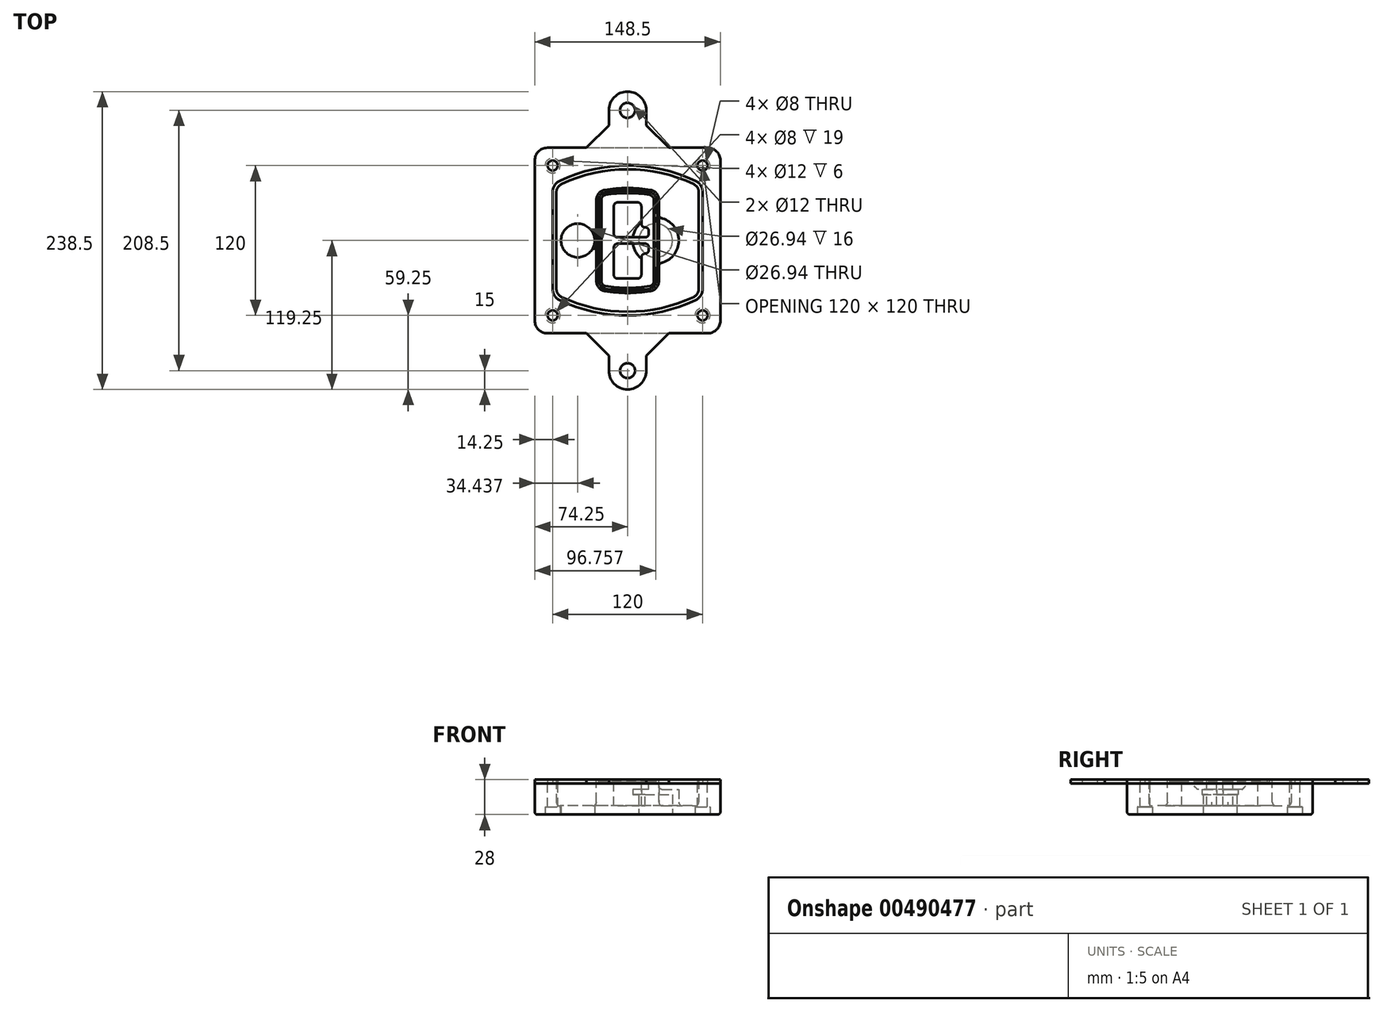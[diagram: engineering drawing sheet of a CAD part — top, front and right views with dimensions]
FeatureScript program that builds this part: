
annotation { "Feature Type Name" : "Feature", "Feature Type Description" : "" }
export const myFeature = defineFeature(function(context is Context, id is Id, definition is map)
    precondition{}
    {
        {
            var Q0;
            Q0=qCreatedBy(makeId("Top.planeOp"),FACE);
            var sketch = newSketch(context, id + "F0", { "sketchPlane" : qUnion([Q0])});
            skPoint(sketch, "E0.rect.middle", {"position": v(0, 0) * mm});
            skLineSegment(sketch, "E1.bottom", {"start": v(-64.25, -74.25) * mm, "end": v(64.25, -74.25) * mm});
            skLineSegment(sketch, "E1.top", {"start": v(-64.25, 74.25) * mm, "end": v(64.25, 74.25) * mm});
            skLineSegment(sketch, "E1.left", {"start": v(-74.25, -64.25) * mm, "end": v(-74.25, 64.25) * mm});
            skLineSegment(sketch, "E1.right", {"start": v(74.25, -64.25) * mm, "end": v(74.25, 64.25) * mm});
            skLineSegment(sketch, "E2", {"start": v(-74.25, 74.25) * mm, "end": v(74.25, -74.25) * mm, "construction": true});
            skLineSegment(sketch, "E3", {"start": v(74.25, 74.25) * mm, "end": v(-74.25, -74.25) * mm, "construction": true});
            skCircle(sketch, "E4", {"center": v(-60, 60) * mm, "radius": 4 * mm});
            skCircle(sketch, "E5", {"center": v(60, 60) * mm, "radius": 4 * mm});
            skCircle(sketch, "E6", {"center": v(60, -60) * mm, "radius": 4 * mm});
            skCircle(sketch, "E7", {"center": v(-60, -60) * mm, "radius": 4 * mm});
            skLineSegment(sketch, "E8", {"start": v(-60, 60) * mm, "end": v(60, 60) * mm, "construction": true});
            skLineSegment(sketch, "E9", {"start": v(60, 60) * mm, "end": v(60, -60) * mm, "construction": true});
            skLineSegment(sketch, "E10", {"start": v(60, -60) * mm, "end": v(-60, -60) * mm, "construction": true});
            skLineSegment(sketch, "E11", {"start": v(-60, -60) * mm, "end": v(-60, 60) * mm, "construction": true});
            skLineSegment(sketch, "E12", {"start": v(-60, 38.83) * mm, "end": v(-60, -38.83) * mm});
            skLineSegment(sketch, "E13", {"start": v(60, 38.83) * mm, "end": v(60, -38.83) * mm});
            skArc(sketch, "E14", {"start": v(54.26, 47.88) * mm, "mid": v(0, 60) * mm, "end": v(-54.26, 47.88) * mm});
            skArc(sketch, "E15", {"start": v(-54.26, -47.88) * mm, "mid": v(0, -60) * mm, "end": v(54.26, -47.88) * mm});
            skLineSegment(sketch, "E16", {"start": v(-60, 0) * mm, "end": v(60, 0) * mm, "construction": true});
            skPoint(sketch, "E17.visualSharp", {"position": v(-60, -45) * mm});
            skArc(sketch, "E17.filletArc", {"start": v(-60, -38.83) * mm, "mid": v(-58.44, -44.2) * mm, "end": v(-54.26, -47.88) * mm});
            skPoint(sketch, "E18.visualSharp", {"position": v(-60, 45) * mm});
            skArc(sketch, "E18.filletArc", {"start": v(-54.26, 47.88) * mm, "mid": v(-58.44, 44.2) * mm, "end": v(-60, 38.83) * mm});
            skPoint(sketch, "E19.visualSharp", {"position": v(60, 45) * mm});
            skArc(sketch, "E19.filletArc", {"start": v(60, 38.83) * mm, "mid": v(58.44, 44.2) * mm, "end": v(54.26, 47.88) * mm});
            skPoint(sketch, "E20.visualSharp", {"position": v(60, -45) * mm});
            skArc(sketch, "E20.filletArc", {"start": v(54.26, -47.88) * mm, "mid": v(58.44, -44.2) * mm, "end": v(60, -38.83) * mm});
            skPoint(sketch, "E21.visualSharp", {"position": v(-74.25, 74.25) * mm});
            skArc(sketch, "E21.filletArc", {"start": v(-64.25, 74.25) * mm, "mid": v(-71.32, 71.32) * mm, "end": v(-74.25, 64.25) * mm});
            skPoint(sketch, "E22.visualSharp", {"position": v(74.25, 74.25) * mm});
            skArc(sketch, "E22.filletArc", {"start": v(74.25, 64.25) * mm, "mid": v(71.32, 71.32) * mm, "end": v(64.25, 74.25) * mm});
            skPoint(sketch, "E23.visualSharp", {"position": v(74.25, -74.25) * mm});
            skArc(sketch, "E23.filletArc", {"start": v(64.25, -74.25) * mm, "mid": v(71.32, -71.32) * mm, "end": v(74.25, -64.25) * mm});
            skPoint(sketch, "E24.visualSharp", {"position": v(-74.25, -74.25) * mm});
            skArc(sketch, "E24.filletArc", {"start": v(-74.25, -64.25) * mm, "mid": v(-71.32, -71.32) * mm, "end": v(-64.25, -74.25) * mm});
            skArc(sketch, "E25.0", {"start": v(57, 38.83) * mm, "mid": v(55.9, 42.58) * mm, "end": v(52.98, 45.17) * mm});
            skLineSegment(sketch, "E25.1", {"start": v(57, 38.83) * mm, "end": v(57, -38.83) * mm});
            skArc(sketch, "E25.2", {"start": v(52.98, -45.17) * mm, "mid": v(55.9, -42.58) * mm, "end": v(57, -38.83) * mm});
            skArc(sketch, "E25.3", {"start": v(-52.98, -45.17) * mm, "mid": v(0, -57) * mm, "end": v(52.98, -45.17) * mm});
            skArc(sketch, "E25.4", {"start": v(-57, -38.83) * mm, "mid": v(-55.9, -42.58) * mm, "end": v(-52.98, -45.17) * mm});
            skArc(sketch, "E25.5", {"start": v(52.98, 45.17) * mm, "mid": v(0, 57) * mm, "end": v(-52.98, 45.17) * mm});
            skLineSegment(sketch, "E25.6", {"start": v(-57, 38.83) * mm, "end": v(-57, -38.83) * mm});
            skArc(sketch, "E25.7", {"start": v(-52.98, 45.17) * mm, "mid": v(-55.9, 42.58) * mm, "end": v(-57, 38.83) * mm});
            skArc(sketch, "E26.0", {"start": v(-55.96, 51.5) * mm, "mid": v(-61.82, 46.33) * mm, "end": v(-64, 38.83) * mm});
            skArc(sketch, "E26.1", {"start": v(55.96, 51.5) * mm, "mid": v(0, 64) * mm, "end": v(-55.96, 51.5) * mm});
            skArc(sketch, "E26.2", {"start": v(64, 38.83) * mm, "mid": v(61.82, 46.33) * mm, "end": v(55.96, 51.5) * mm});
            skLineSegment(sketch, "E26.3", {"start": v(64, 38.83) * mm, "end": v(64, -38.83) * mm});
            skArc(sketch, "E26.4", {"start": v(55.96, -51.5) * mm, "mid": v(61.82, -46.33) * mm, "end": v(64, -38.83) * mm});
            skLineSegment(sketch, "E26.5", {"start": v(-64, 38.83) * mm, "end": v(-64, -38.83) * mm});
            skArc(sketch, "E26.6", {"start": v(-55.96, -51.5) * mm, "mid": v(0, -64) * mm, "end": v(55.96, -51.5) * mm});
            skArc(sketch, "E26.7", {"start": v(-64, -38.83) * mm, "mid": v(-61.82, -46.33) * mm, "end": v(-55.96, -51.5) * mm});
            skSolve(sketch);
        }
        {
            var Q0;
            Q0=makeQuery(id+"F0.imprint","IMPRINT",FACE,{"disambiguationData":[TD([[makeQuery(id+"F0.imprint","IMPRINT",EDGE,{"derivedFrom":sQuery(id+"F0.wireOp",EDGE,"E1.bottom")}),1.0]])]});
            var Q1;
            Q1=makeQuery(id+"F0.imprint","IMPRINT",FACE,{"disambiguationData":[TD([[makeQuery(id+"F0.imprint","IMPRINT",EDGE,{"derivedFrom":sQuery(id+"F0.wireOp",EDGE,"E12")}),1.0]])]});
            var Q2;
            Q2=makeQuery(id+"F0.imprint","IMPRINT",FACE,{"disambiguationData":[TD([[makeQuery(id+"F0.imprint","IMPRINT",EDGE,{"derivedFrom":sQuery(id+"F0.wireOp",EDGE,"E25.0")}),1.0]])]});
            var Q3;
            Q3=makeQuery(id+"F0.imprint","IMPRINT",FACE,{"disambiguationData":[TD([[makeQuery(id+"F0.imprint","IMPRINT",EDGE,{"derivedFrom":sQuery(id+"F0.wireOp",EDGE,"E12")}),-1.0]])]});
            extrude(context, id + "F1", {"entities" : qUnion([Q0, Q1, Q2, Q3]), "oppositeDirection" : true, "depth" : 25 * mm});
        }
        {
            var Q0;
            Q0=makeQuery(id+"F0.imprint","IMPRINT",FACE,{"disambiguationData":[TD([[makeQuery(id+"F0.imprint","IMPRINT",EDGE,{"derivedFrom":sQuery(id+"F0.wireOp",EDGE,"E12")}),1.0]])]});
            extrude(context, id + "F2", {"entities" : qUnion([Q0]), "operationType" : NewBodyOperationType.ADD, "depth" : 3 * mm});
        }
        {
            var Q0;
            Q0=makeQuery(id+"F0.imprint","IMPRINT",FACE,{"disambiguationData":[TD([[makeQuery(id+"F0.imprint","IMPRINT",EDGE,{"derivedFrom":sQuery(id+"F0.wireOp",EDGE,"E25.0")}),1.0]])]});
            extrude(context, id + "F3", {"entities" : qUnion([Q0]), "operationType" : NewBodyOperationType.REMOVE, "oppositeDirection" : true, "depth" : 18 * mm});
        }
        {
            var Q0;
            Q0=makeQuery(id+"F2.opExtrude","CAP_FACE",FACE,{"disambiguationData":[OSD([sQuery(id+"F0.wireOp",EDGE,"E12"),sQuery(id+"F0.wireOp",EDGE,"E13"),sQuery(id+"F0.wireOp",EDGE,"E14"),sQuery(id+"F0.wireOp",EDGE,"E15"),sQuery(id+"F0.wireOp",EDGE,"E17.filletArc"),sQuery(id+"F0.wireOp",EDGE,"E18.filletArc"),sQuery(id+"F0.wireOp",EDGE,"E19.filletArc"),sQuery(id+"F0.wireOp",EDGE,"E20.filletArc"),sQuery(id+"F0.wireOp",EDGE,"E25.0"),sQuery(id+"F0.wireOp",EDGE,"E25.1"),sQuery(id+"F0.wireOp",EDGE,"E25.2"),sQuery(id+"F0.wireOp",EDGE,"E25.3"),sQuery(id+"F0.wireOp",EDGE,"E25.4"),sQuery(id+"F0.wireOp",EDGE,"E25.5"),sQuery(id+"F0.wireOp",EDGE,"E25.6"),sQuery(id+"F0.wireOp",EDGE,"E25.7")])],"isStart":false});
            var sketch = newSketch(context, id + "F4", { "sketchPlane" : qUnion([Q0])});
            skArc(sketch, "E27.0", {"start": v(-18.34, -40.45) * mm, "mid": v(0, -42) * mm, "end": v(18.34, -40.45) * mm});
            skArc(sketch, "E28.0", {"start": v(18.34, 40.45) * mm, "mid": v(0, 42) * mm, "end": v(-18.34, 40.45) * mm});
            skLineSegment(sketch, "E29", {"start": v(-25, 32.57) * mm, "end": v(-25, -32.57) * mm});
            skLineSegment(sketch, "E30", {"start": v(25, 32.57) * mm, "end": v(25, -32.57) * mm});
            skLineSegment(sketch, "E31", {"start": v(-25, 39.1) * mm, "end": v(25, 39.1) * mm, "construction": true});
            skLineSegment(sketch, "E32", {"start": v(-25, -39.1) * mm, "end": v(25, -39.1) * mm, "construction": true});
            skPoint(sketch, "E33.visualSharp", {"position": v(-25, 39.1) * mm});
            skArc(sketch, "E33.filletArc", {"start": v(-18.34, 40.45) * mm, "mid": v(-23.11, 37.73) * mm, "end": v(-25, 32.57) * mm});
            skPoint(sketch, "E34.visualSharp", {"position": v(25, 39.1) * mm});
            skArc(sketch, "E34.filletArc", {"start": v(25, 32.57) * mm, "mid": v(23.11, 37.73) * mm, "end": v(18.34, 40.45) * mm});
            skPoint(sketch, "E35.visualSharp", {"position": v(25, -39.1) * mm});
            skArc(sketch, "E35.filletArc", {"start": v(18.34, -40.45) * mm, "mid": v(23.11, -37.73) * mm, "end": v(25, -32.57) * mm});
            skPoint(sketch, "E36.visualSharp", {"position": v(-25, -39.1) * mm});
            skArc(sketch, "E36.filletArc", {"start": v(-25, -32.57) * mm, "mid": v(-23.11, -37.73) * mm, "end": v(-18.34, -40.45) * mm});
            skArc(sketch, "E37.0", {"start": v(52.98, 45.17) * mm, "mid": v(0, 57) * mm, "end": v(-52.98, 45.17) * mm});
            skArc(sketch, "E37.1", {"start": v(-52.98, 45.17) * mm, "mid": v(-55.9, 42.58) * mm, "end": v(-57, 38.83) * mm});
            skLineSegment(sketch, "E37.2", {"start": v(-57, 38.83) * mm, "end": v(-57, -38.83) * mm});
            skArc(sketch, "E37.3", {"start": v(-57, -38.83) * mm, "mid": v(-55.9, -42.58) * mm, "end": v(-52.98, -45.17) * mm});
            skArc(sketch, "E37.4", {"start": v(-52.98, -45.17) * mm, "mid": v(0, -57) * mm, "end": v(52.98, -45.17) * mm});
            skArc(sketch, "E37.5", {"start": v(52.98, -45.17) * mm, "mid": v(55.9, -42.58) * mm, "end": v(57, -38.83) * mm});
            skLineSegment(sketch, "E37.6", {"start": v(57, 38.83) * mm, "end": v(57, -38.83) * mm});
            skArc(sketch, "E37.7", {"start": v(57, 38.83) * mm, "mid": v(55.9, 42.58) * mm, "end": v(52.98, 45.17) * mm});
            skLineSegment(sketch, "E38.0", {"start": v(23, 32.57) * mm, "end": v(23, -32.57) * mm});
            skArc(sketch, "E38.1", {"start": v(18, -38.48) * mm, "mid": v(21.58, -36.44) * mm, "end": v(23, -32.57) * mm});
            skArc(sketch, "E38.2", {"start": v(-18, -38.48) * mm, "mid": v(0, -40) * mm, "end": v(18, -38.48) * mm});
            skArc(sketch, "E38.3", {"start": v(-23, -32.57) * mm, "mid": v(-21.58, -36.44) * mm, "end": v(-18, -38.48) * mm});
            skLineSegment(sketch, "E38.4", {"start": v(-23, 32.57) * mm, "end": v(-23, -32.57) * mm});
            skArc(sketch, "E38.5", {"start": v(23, 32.57) * mm, "mid": v(21.58, 36.44) * mm, "end": v(18, 38.48) * mm});
            skArc(sketch, "E38.6", {"start": v(-18, 38.48) * mm, "mid": v(-21.58, 36.44) * mm, "end": v(-23, 32.57) * mm});
            skArc(sketch, "E38.7", {"start": v(18, 38.48) * mm, "mid": v(0, 40) * mm, "end": v(-18, 38.48) * mm});
            skArc(sketch, "E39.0", {"start": v(21, 32.57) * mm, "mid": v(20.06, 35.15) * mm, "end": v(17.67, 36.5) * mm});
            skLineSegment(sketch, "E39.1", {"start": v(21, 32.57) * mm, "end": v(21, -32.57) * mm});
            skArc(sketch, "E39.2", {"start": v(17.67, -36.5) * mm, "mid": v(20.06, -35.15) * mm, "end": v(21, -32.57) * mm});
            skArc(sketch, "E39.3", {"start": v(-17.67, -36.5) * mm, "mid": v(0, -38) * mm, "end": v(17.67, -36.5) * mm});
            skArc(sketch, "E39.4", {"start": v(-21, -32.57) * mm, "mid": v(-20.06, -35.15) * mm, "end": v(-17.67, -36.5) * mm});
            skArc(sketch, "E39.5", {"start": v(17.67, 36.5) * mm, "mid": v(0, 38) * mm, "end": v(-17.67, 36.5) * mm});
            skLineSegment(sketch, "E39.6", {"start": v(-21, 32.57) * mm, "end": v(-21, -32.57) * mm});
            skArc(sketch, "E39.7", {"start": v(-17.67, 36.5) * mm, "mid": v(-20.06, 35.15) * mm, "end": v(-21, 32.57) * mm});
            skLineSegment(sketch, "E40", {"start": v(-25, 0) * mm, "end": v(25, 0) * mm, "construction": true});
            skLineSegment(sketch, "E41", {"start": v(-11, 5.5) * mm, "end": v(-11, 27.5) * mm});
            skLineSegment(sketch, "E42", {"start": v(-8, 30.5) * mm, "end": v(8, 30.5) * mm});
            skLineSegment(sketch, "E43", {"start": v(11, 27.5) * mm, "end": v(11, 13.5) * mm});
            skLineSegment(sketch, "E44", {"start": v(14, 10.5) * mm, "end": v(14, 10.5) * mm});
            skLineSegment(sketch, "E45", {"start": v(17, 7.5) * mm, "end": v(17, 5.5) * mm});
            skLineSegment(sketch, "E46", {"start": v(14, 2.5) * mm, "end": v(-8, 2.5) * mm});
            skPoint(sketch, "E47.visualSharp", {"position": v(-11, 30.5) * mm});
            skArc(sketch, "E47.filletArc", {"start": v(-8, 30.5) * mm, "mid": v(-10.12, 29.62) * mm, "end": v(-11, 27.5) * mm});
            skPoint(sketch, "E48.visualSharp", {"position": v(11, 30.5) * mm});
            skArc(sketch, "E48.filletArc", {"start": v(11, 27.5) * mm, "mid": v(10.12, 29.62) * mm, "end": v(8, 30.5) * mm});
            skPoint(sketch, "E49.visualSharp", {"position": v(11, 10.5) * mm});
            skArc(sketch, "E49.filletArc", {"start": v(11, 13.5) * mm, "mid": v(11.88, 11.38) * mm, "end": v(14, 10.5) * mm});
            skPoint(sketch, "E50.visualSharp", {"position": v(17, 10.5) * mm});
            skArc(sketch, "E50.filletArc", {"start": v(17, 7.5) * mm, "mid": v(16.12, 9.62) * mm, "end": v(14, 10.5) * mm});
            skPoint(sketch, "E51.visualSharp", {"position": v(17, 2.5) * mm});
            skArc(sketch, "E51.filletArc", {"start": v(14, 2.5) * mm, "mid": v(16.12, 3.38) * mm, "end": v(17, 5.5) * mm});
            skPoint(sketch, "E52.visualSharp", {"position": v(-11, 2.5) * mm});
            skArc(sketch, "E52.filletArc", {"start": v(-11, 5.5) * mm, "mid": v(-10.12, 3.38) * mm, "end": v(-8, 2.5) * mm});
            skLineSegment(sketch, "E53.0.MirrorCS", {"start": v(14, -2.5) * mm, "end": v(-8, -2.5) * mm});
            skArc(sketch, "E54.0.MirrorCS", {"start": v(-11, -5.5) * mm, "mid": v(-10.12, -3.38) * mm, "end": v(-8, -2.5) * mm});
            skLineSegment(sketch, "E55.0.MirrorCS", {"start": v(-11, -5.5) * mm, "end": v(-11, -27.5) * mm});
            skArc(sketch, "E56.0.MirrorCS", {"start": v(-8, -30.5) * mm, "mid": v(-10.12, -29.62) * mm, "end": v(-11, -27.5) * mm});
            skLineSegment(sketch, "E57.0.MirrorCS", {"start": v(-8, -30.5) * mm, "end": v(8, -30.5) * mm});
            skArc(sketch, "E58.0.MirrorCS", {"start": v(11, -27.5) * mm, "mid": v(10.12, -29.62) * mm, "end": v(8, -30.5) * mm});
            skLineSegment(sketch, "E59.0.MirrorCS", {"start": v(11, -27.5) * mm, "end": v(11, -13.5) * mm});
            skArc(sketch, "E60.0.MirrorCS", {"start": v(11, -13.5) * mm, "mid": v(11.88, -11.38) * mm, "end": v(14, -10.5) * mm});
            skArc(sketch, "E61.0.MirrorCS", {"start": v(17, -7.5) * mm, "mid": v(16.12, -9.62) * mm, "end": v(14, -10.5) * mm});
            skLineSegment(sketch, "E62.0.MirrorCS", {"start": v(17, -7.5) * mm, "end": v(17, -5.5) * mm});
            skArc(sketch, "E63.0.MirrorCS", {"start": v(14, -2.5) * mm, "mid": v(16.12, -3.38) * mm, "end": v(17, -5.5) * mm});
            skSolve(sketch);
        }
        {
            var Q0;
            Q0=makeQuery(id+"F4.imprint","IMPRINT",FACE,{"disambiguationData":[TD([[makeQuery(id+"F4.imprint","IMPRINT",EDGE,{"derivedFrom":sQuery(id+"F4.wireOp",EDGE,"E27.0")}),1.0]])]});
            var Q1;
            Q1=makeQuery(id+"F4.imprint","IMPRINT",FACE,{"disambiguationData":[TD([[makeQuery(id+"F4.imprint","IMPRINT",EDGE,{"derivedFrom":sQuery(id+"F4.wireOp",EDGE,"E38.0")}),-1.0]])]});
            var Q2;
            Q2=makeQuery(id+"F4.imprint","IMPRINT",FACE,{"disambiguationData":[TD([[makeQuery(id+"F4.imprint","IMPRINT",EDGE,{"derivedFrom":sQuery(id+"F4.wireOp",EDGE,"E39.0")}),1.0]])]});
            extrude(context, id + "F5", {"entities" : qUnion([Q0, Q1, Q2]), "operationType" : NewBodyOperationType.ADD, "endBound" : BoundingType.UP_TO_NEXT, "oppositeDirection" : true, "depth" : 25 * mm});
        }
        {
            var Q0;
            Q0=makeQuery(id+"F4.imprint","IMPRINT",FACE,{"disambiguationData":[TD([[makeQuery(id+"F4.imprint","IMPRINT",EDGE,{"derivedFrom":sQuery(id+"F4.wireOp",EDGE,"E38.0")}),-1.0]])]});
            extrude(context, id + "F6", {"entities" : qUnion([Q0]), "operationType" : NewBodyOperationType.REMOVE, "oppositeDirection" : true, "depth" : 2 * mm});
        }
        {
            var Q0;
            Q0=makeQuery(id+"F1.opExtrude","CAP_FACE",FACE,{"disambiguationData":[OSD([sQuery(id+"F0.wireOp",EDGE,"E1.bottom"),sQuery(id+"F0.wireOp",EDGE,"E1.top"),sQuery(id+"F0.wireOp",EDGE,"E1.left"),sQuery(id+"F0.wireOp",EDGE,"E1.right"),sQuery(id+"F0.wireOp",EDGE,"E4"),sQuery(id+"F0.wireOp",EDGE,"E5"),sQuery(id+"F0.wireOp",EDGE,"E6"),sQuery(id+"F0.wireOp",EDGE,"E7"),sQuery(id+"F0.wireOp",EDGE,"E21.filletArc"),sQuery(id+"F0.wireOp",EDGE,"E22.filletArc"),sQuery(id+"F0.wireOp",EDGE,"E23.filletArc"),sQuery(id+"F0.wireOp",EDGE,"E24.filletArc")])],"isStart":false});
            var sketch = newSketch(context, id + "F7", { "sketchPlane" : qUnion([Q0])});
            skCircle(sketch, "E64", {"center": v(22.5, 0) * mm, "radius": 13.47 * mm});
            skCircle(sketch, "E65", {"center": v(-39.81, 0) * mm, "radius": 13.47 * mm});
            skLineSegment(sketch, "E66", {"start": v(74.25, 0) * mm, "end": v(-74.25, 0) * mm});
            skCircle(sketch, "E67", {"center": v(22.5, 0) * mm, "radius": 18.47 * mm});
            skCircle(sketch, "E68", {"center": v(60, -60) * mm, "radius": 6 * mm});
            skCircle(sketch, "E69", {"center": v(-60, -60) * mm, "radius": 6 * mm});
            skCircle(sketch, "E70", {"center": v(-60, 60) * mm, "radius": 6 * mm});
            skCircle(sketch, "E71", {"center": v(60, 60) * mm, "radius": 6 * mm});
            skSolve(sketch);
        }
        {
            var Q0;
            {var subQ1=sQuery(id+"F7.wireOp",EDGE,"E66");var subQ4=sQuery(id+"F7.wireOp",EDGE,"E64");var subQ6=makeQuery(id+"F7.imprint","INTERSECT",VERTEX,{"disambiguationData":[OD(0.0)],"derivedFrom":[subQ4,subQ1]});Q0=makeQuery(id+"F7.imprint","IMPRINT",FACE,{"disambiguationData":[TD([[makeQuery(id+"F7.imprint","IMPRINT",EDGE,{"disambiguationData":[TD([[subQ6,-1.0]])],"derivedFrom":subQ4}),-1.0]])]});}
            var Q1;
            {var subQ0=sQuery(id+"F7.wireOp",EDGE,"E66");var subQ1=sQuery(id+"F7.wireOp",EDGE,"E64");var subQ3=makeQuery(id+"F7.imprint","INTERSECT",VERTEX,{"disambiguationData":[OD(0.0)],"derivedFrom":[subQ1,subQ0]});Q1=makeQuery(id+"F7.imprint","IMPRINT",FACE,{"disambiguationData":[TD([[makeQuery(id+"F7.imprint","IMPRINT",EDGE,{"disambiguationData":[TD([[subQ3,-1.0]])],"derivedFrom":subQ1}),1.0]])]});}
            var Q2;
            {var subQ0=sQuery(id+"F7.wireOp",EDGE,"E66");var subQ1=sQuery(id+"F7.wireOp",EDGE,"E64");var subQ3=makeQuery(id+"F7.imprint","INTERSECT",VERTEX,{"disambiguationData":[OD(0.0)],"derivedFrom":[subQ1,subQ0]});Q2=makeQuery(id+"F7.imprint","IMPRINT",FACE,{"disambiguationData":[TD([[makeQuery(id+"F7.imprint","IMPRINT",EDGE,{"disambiguationData":[TD([[subQ3,1.0]])],"derivedFrom":subQ1}),1.0]])]});}
            var Q3;
            {var subQ1=sQuery(id+"F7.wireOp",EDGE,"E66");var subQ4=sQuery(id+"F7.wireOp",EDGE,"E64");var subQ6=makeQuery(id+"F7.imprint","INTERSECT",VERTEX,{"disambiguationData":[OD(0.0)],"derivedFrom":[subQ4,subQ1]});Q3=makeQuery(id+"F7.imprint","IMPRINT",FACE,{"disambiguationData":[TD([[makeQuery(id+"F7.imprint","IMPRINT",EDGE,{"disambiguationData":[TD([[subQ6,1.0]])],"derivedFrom":subQ4}),-1.0]])]});}
            extrude(context, id + "F8", {"entities" : qUnion([Q0, Q1, Q2, Q3]), "operationType" : NewBodyOperationType.ADD, "oppositeDirection" : true, "depth" : 20 * mm});
        }
        {
            var Q0;
            {var subQ0=sQuery(id+"F7.wireOp",EDGE,"E66");var subQ1=sQuery(id+"F7.wireOp",EDGE,"E64");var subQ3=makeQuery(id+"F7.imprint","INTERSECT",VERTEX,{"disambiguationData":[OD(0.0)],"derivedFrom":[subQ1,subQ0]});Q0=makeQuery(id+"F7.imprint","IMPRINT",FACE,{"disambiguationData":[TD([[makeQuery(id+"F7.imprint","IMPRINT",EDGE,{"disambiguationData":[TD([[subQ3,-1.0]])],"derivedFrom":subQ1}),1.0]])]});}
            var Q1;
            {var subQ0=sQuery(id+"F7.wireOp",EDGE,"E66");var subQ1=sQuery(id+"F7.wireOp",EDGE,"E64");var subQ3=makeQuery(id+"F7.imprint","INTERSECT",VERTEX,{"disambiguationData":[OD(0.0)],"derivedFrom":[subQ1,subQ0]});Q1=makeQuery(id+"F7.imprint","IMPRINT",FACE,{"disambiguationData":[TD([[makeQuery(id+"F7.imprint","IMPRINT",EDGE,{"disambiguationData":[TD([[subQ3,1.0]])],"derivedFrom":subQ1}),1.0]])]});}
            extrude(context, id + "F9", {"entities" : qUnion([Q0, Q1]), "operationType" : NewBodyOperationType.REMOVE, "oppositeDirection" : true, "depth" : 16 * mm});
        }
        {
            var Q0;
            {var subQ0=sQuery(id+"F7.wireOp",EDGE,"E66");var subQ1=sQuery(id+"F7.wireOp",EDGE,"E65");var subQ3=makeQuery(id+"F7.imprint","INTERSECT",VERTEX,{"disambiguationData":[OD(0.0)],"derivedFrom":[subQ1,subQ0]});Q0=makeQuery(id+"F7.imprint","IMPRINT",FACE,{"disambiguationData":[TD([[makeQuery(id+"F7.imprint","IMPRINT",EDGE,{"disambiguationData":[TD([[subQ3,-1.0]])],"derivedFrom":subQ1}),1.0]])]});}
            var Q1;
            {var subQ0=sQuery(id+"F7.wireOp",EDGE,"E66");var subQ1=sQuery(id+"F7.wireOp",EDGE,"E65");var subQ3=makeQuery(id+"F7.imprint","INTERSECT",VERTEX,{"disambiguationData":[OD(0.0)],"derivedFrom":[subQ1,subQ0]});Q1=makeQuery(id+"F7.imprint","IMPRINT",FACE,{"disambiguationData":[TD([[makeQuery(id+"F7.imprint","IMPRINT",EDGE,{"disambiguationData":[TD([[subQ3,1.0]])],"derivedFrom":subQ1}),1.0]])]});}
            extrude(context, id + "F10", {"entities" : qUnion([Q0, Q1]), "operationType" : NewBodyOperationType.REMOVE, "oppositeDirection" : true, "depth" : 25 * mm});
        }
        {
            var Q0;
            Q0=makeQuery(id+"F7.imprint","IMPRINT",FACE,{"disambiguationData":[TD([[makeQuery(id+"F7.imprint","IMPRINT",EDGE,{"derivedFrom":sQuery(id+"F7.wireOp",EDGE,"E68")}),1.0]])]});
            var Q1;
            Q1=makeQuery(id+"F7.imprint","IMPRINT",FACE,{"disambiguationData":[TD([[makeQuery(id+"F7.imprint","IMPRINT",EDGE,{"derivedFrom":makeQuery(id+"F1.opExtrude","CAP_EDGE",EDGE,{"disambiguationData":[OSD([sQuery(id+"F0.wireOp",EDGE,"E5")])],"isStart":false})}),-1.0]])]});
            var Q2;
            Q2=makeQuery(id+"F7.imprint","IMPRINT",FACE,{"disambiguationData":[TD([[makeQuery(id+"F7.imprint","IMPRINT",EDGE,{"derivedFrom":sQuery(id+"F7.wireOp",EDGE,"E69")}),1.0]])]});
            var Q3;
            Q3=makeQuery(id+"F7.imprint","IMPRINT",FACE,{"disambiguationData":[TD([[makeQuery(id+"F7.imprint","IMPRINT",EDGE,{"derivedFrom":makeQuery(id+"F1.opExtrude","CAP_EDGE",EDGE,{"disambiguationData":[OSD([sQuery(id+"F0.wireOp",EDGE,"E4")])],"isStart":false})}),-1.0]])]});
            var Q4;
            Q4=makeQuery(id+"F7.imprint","IMPRINT",FACE,{"disambiguationData":[TD([[makeQuery(id+"F7.imprint","IMPRINT",EDGE,{"derivedFrom":sQuery(id+"F7.wireOp",EDGE,"E70")}),1.0]])]});
            var Q5;
            Q5=makeQuery(id+"F7.imprint","IMPRINT",FACE,{"disambiguationData":[TD([[makeQuery(id+"F7.imprint","IMPRINT",EDGE,{"derivedFrom":makeQuery(id+"F1.opExtrude","CAP_EDGE",EDGE,{"disambiguationData":[OSD([sQuery(id+"F0.wireOp",EDGE,"E7")])],"isStart":false})}),-1.0]])]});
            var Q6;
            Q6=makeQuery(id+"F7.imprint","IMPRINT",FACE,{"disambiguationData":[TD([[makeQuery(id+"F7.imprint","IMPRINT",EDGE,{"derivedFrom":sQuery(id+"F7.wireOp",EDGE,"E71")}),1.0]])]});
            var Q7;
            Q7=makeQuery(id+"F7.imprint","IMPRINT",FACE,{"disambiguationData":[TD([[makeQuery(id+"F7.imprint","IMPRINT",EDGE,{"derivedFrom":makeQuery(id+"F1.opExtrude","CAP_EDGE",EDGE,{"disambiguationData":[OSD([sQuery(id+"F0.wireOp",EDGE,"E6")])],"isStart":false})}),-1.0]])]});
            extrude(context, id + "F11", {"entities" : qUnion([Q0, Q1, Q2, Q3, Q4, Q5, Q6, Q7]), "operationType" : NewBodyOperationType.REMOVE, "oppositeDirection" : true, "depth" : 6 * mm});
        }
        {
            var Q0;
            Q0=makeQuery(id+"F9.boolean.opBoolean","COPY",FACE,{"derivedFrom":makeQuery(id+"F9.opExtrude","CAP_FACE",FACE,{"disambiguationData":[OSD([sQuery(id+"F7.wireOp",EDGE,"E64")])],"isStart":false})});
            var sketch = newSketch(context, id + "F12", { "sketchPlane" : qUnion([Q0])});
            skArc(sketch, "E72.0", {"start": v(11, 14.45) * mm, "mid": v(6.45, 9.13) * mm, "end": v(4.2, 2.5) * mm});
            skArc(sketch, "E72.1", {"start": v(4.2, -2.5) * mm, "mid": v(6.45, -9.13) * mm, "end": v(11, -14.45) * mm});
            skLineSegment(sketch, "E73", {"start": v(4.2, -2.5) * mm, "end": v(14, -2.5) * mm});
            skLineSegment(sketch, "E74.0", {"start": v(14, 2.5) * mm, "end": v(4.2, 2.5) * mm});
            skArc(sketch, "E74.1", {"start": v(14, 2.5) * mm, "mid": v(16.12, 3.38) * mm, "end": v(17, 5.5) * mm});
            skLineSegment(sketch, "E74.2", {"start": v(17, 7.5) * mm, "end": v(17, 5.5) * mm});
            skArc(sketch, "E74.3", {"start": v(17, 7.5) * mm, "mid": v(16.12, 9.62) * mm, "end": v(14, 10.5) * mm});
            skArc(sketch, "E74.4", {"start": v(11, 13.5) * mm, "mid": v(11.88, 11.38) * mm, "end": v(14, 10.5) * mm});
            skLineSegment(sketch, "E74.5", {"start": v(11, 14.45) * mm, "end": v(11, 13.5) * mm});
            skLineSegment(sketch, "E74.7", {"start": v(14, -2.5) * mm, "end": v(4.2, -2.5) * mm});
            skArc(sketch, "E74.8", {"start": v(14, -2.5) * mm, "mid": v(16.12, -3.38) * mm, "end": v(17, -5.5) * mm});
            skLineSegment(sketch, "E74.9", {"start": v(17, -7.5) * mm, "end": v(17, -5.5) * mm});
            skArc(sketch, "E74.10", {"start": v(17, -7.5) * mm, "mid": v(16.12, -9.62) * mm, "end": v(14, -10.5) * mm});
            skArc(sketch, "E74.11", {"start": v(11, -13.5) * mm, "mid": v(11.88, -11.38) * mm, "end": v(14, -10.5) * mm});
            skLineSegment(sketch, "E74.12", {"start": v(11, -14.45) * mm, "end": v(11, -13.5) * mm});
            skPoint(sketch, "E75.orphan", {"position": v(11, -27.5) * mm});
            skPoint(sketch, "E76.orphan", {"position": v(-8, -2.5) * mm});
            skPoint(sketch, "E77.orphan", {"position": v(-8, 2.5) * mm});
            skPoint(sketch, "E78.orphan", {"position": v(11, 27.5) * mm});
            skSolve(sketch);
        }
        {
            var Q0;
            {var subQ7=sQuery(id+"F12.wireOp",EDGE,"E72.0");var subQ14=sQuery(id+"F12.wireOp",EDGE,"E72.1");var subQ16=sQuery(id+"F12.wireOp",EDGE,"E74.1");var subQ18=sQuery(id+"F12.wireOp",EDGE,"E74.8");Q0=qUnion([makeQuery(id+"F12.imprint","IMPRINT",FACE,{"disambiguationData":[TD([[makeQuery(id+"F12.imprint","IMPRINT",EDGE,{"derivedFrom":subQ7}),1.0]])]}),makeQuery(id+"F12.imprint","IMPRINT",FACE,{"disambiguationData":[TD([[makeQuery(id+"F12.imprint","IMPRINT",EDGE,{"derivedFrom":subQ14}),1.0]])]}),makeQuery(id+"F12.imprint","IMPRINT",FACE,{"disambiguationData":[TD([[makeQuery(id+"F12.imprint","IMPRINT",EDGE,{"derivedFrom":subQ16}),1.0]])]}),makeQuery(id+"F12.imprint","IMPRINT",FACE,{"disambiguationData":[TD([[makeQuery(id+"F12.imprint","IMPRINT",EDGE,{"derivedFrom":subQ18}),-1.0]])]})]);}
            var Q1;
            Q1=makeQuery(id+"F5.boolean.opBoolean","SPLIT",FACE,{"disambiguationData":[TD([makeQuery(id+"F5.opExtrude","SWEPT_FACE",FACE,{"disambiguationData":[OSD([sQuery(id+"F4.wireOp",EDGE,"E41")])]})])],"derivedFrom":makeQuery(id+"F3.boolean.opBoolean","COPY",FACE,{"derivedFrom":makeQuery(id+"F3.opExtrude","CAP_FACE",FACE,{"disambiguationData":[OSD([sQuery(id+"F0.wireOp",EDGE,"E25.0"),sQuery(id+"F0.wireOp",EDGE,"E25.1"),sQuery(id+"F0.wireOp",EDGE,"E25.2"),sQuery(id+"F0.wireOp",EDGE,"E25.3"),sQuery(id+"F0.wireOp",EDGE,"E25.4"),sQuery(id+"F0.wireOp",EDGE,"E25.5"),sQuery(id+"F0.wireOp",EDGE,"E25.6"),sQuery(id+"F0.wireOp",EDGE,"E25.7")])],"isStart":false})})});
            extrude(context, id + "F13", {"entities" : qUnion([Q0]), "operationType" : NewBodyOperationType.REMOVE, "endBound" : BoundingType.UP_TO_SURFACE, "endBoundEntityFace" : qUnion([Q1]), "depth" : 25 * mm});
        }
        {
            var Q0;
            Q0=makeQuery(id+"F3.boolean.opBoolean","COPY",EDGE,{"derivedFrom":makeQuery(id+"F3.opExtrude","CAP_EDGE",EDGE,{"disambiguationData":[OSD([sQuery(id+"F0.wireOp",EDGE,"E25.6")])],"isStart":false})});
            var Q1;
            Q1=makeQuery(id+"F8.boolean.opBoolean","INTERSECT",EDGE,{"derivedFrom":[makeQuery(id+"F5.opExtrude","SWEPT_FACE",FACE,{"disambiguationData":[OSD([sQuery(id+"F4.wireOp",EDGE,"E30")])]}),makeQuery(id+"F8.opExtrude","CAP_FACE",FACE,{"disambiguationData":[OSD([sQuery(id+"F7.wireOp",EDGE,"E67")])],"isStart":false})]});
            var Q2;
            Q2=makeQuery(id+"F8.boolean.opBoolean","INTERSECT",EDGE,{"disambiguationData":[OD(1.0)],"derivedFrom":[makeQuery(id+"F5.opExtrude","SWEPT_FACE",FACE,{"disambiguationData":[OSD([sQuery(id+"F4.wireOp",EDGE,"E30")])]}),makeQuery(id+"F8.opExtrude","SWEPT_FACE",FACE,{"disambiguationData":[OSD([sQuery(id+"F7.wireOp",EDGE,"E67")])]})]});
            var Q3;
            {var subQ0=sQuery(id+"F4.wireOp",EDGE,"E30");Q3=makeQuery(id+"F8.boolean.opBoolean","SPLIT",EDGE,{"disambiguationData":[TD([makeQuery(id+"F5.opExtrude","SWEPT_FACE",FACE,{"disambiguationData":[OSD([sQuery(id+"F4.wireOp",EDGE,"E35.filletArc")])]})])],"derivedFrom":makeQuery(id+"F5.opExtrude","CAP_EDGE",EDGE,{"disambiguationData":[OSD([subQ0])],"isStart":false})});}
            var Q4;
            {var subQ0=sQuery(id+"F0.wireOp",EDGE,"E25.7");var subQ1=sQuery(id+"F0.wireOp",EDGE,"E25.1");var subQ2=sQuery(id+"F0.wireOp",EDGE,"E25.6");var subQ3=sQuery(id+"F0.wireOp",EDGE,"E25.5");var subQ4=sQuery(id+"F0.wireOp",EDGE,"E25.4");var subQ5=sQuery(id+"F0.wireOp",EDGE,"E25.0");var subQ6=sQuery(id+"F0.wireOp",EDGE,"E25.2");var subQ7=sQuery(id+"F0.wireOp",EDGE,"E25.3");Q4=makeQuery(id+"F8.boolean.opBoolean","INTERSECT",EDGE,{"derivedFrom":[makeQuery(id+"F5.boolean.opBoolean","SPLIT",FACE,{"disambiguationData":[TD([makeQuery(id+"F2.opExtrude","SWEPT_FACE",FACE,{"disambiguationData":[OSD([subQ5])]})])],"derivedFrom":makeQuery(id+"F3.boolean.opBoolean","COPY",FACE,{"derivedFrom":makeQuery(id+"F3.opExtrude","CAP_FACE",FACE,{"disambiguationData":[OSD([subQ5,subQ1,subQ6,subQ7,subQ4,subQ3,subQ2,subQ0])],"isStart":false})})}),makeQuery(id+"F8.opExtrude","SWEPT_FACE",FACE,{"disambiguationData":[OSD([sQuery(id+"F7.wireOp",EDGE,"E67")])]})]});}
            var Q5;
            Q5=makeQuery(id+"F8.boolean.opBoolean","INTERSECT",EDGE,{"disambiguationData":[OD(0.0)],"derivedFrom":[makeQuery(id+"F5.opExtrude","SWEPT_FACE",FACE,{"disambiguationData":[OSD([sQuery(id+"F4.wireOp",EDGE,"E30")])]}),makeQuery(id+"F8.opExtrude","SWEPT_FACE",FACE,{"disambiguationData":[OSD([sQuery(id+"F7.wireOp",EDGE,"E67")])]})]});
            fillet(context, id + "F14", {"entities" : qUnion([Q0, Q1, Q2, Q3, Q4, Q5]), "radius" : 3 * mm, "tangentPropagation" : true, "allowEdgeOverflow" : false});
        }
        {
            var Q0;
            Q0=makeQuery(id+"F1.opExtrude","CAP_EDGE",EDGE,{"disambiguationData":[OSD([sQuery(id+"F0.wireOp",EDGE,"E1.bottom")])],"isStart":false});
            fillet(context, id + "F15", {"entities" : qUnion([Q0]), "radius" : 2 * mm, "tangentPropagation" : true, "allowEdgeOverflow" : false});
        }
        {
            var Q0;
            {var subQ0=sQuery(id+"F0.wireOp",EDGE,"E21.filletArc");var subQ1=sQuery(id+"F0.wireOp",EDGE,"E7");var subQ2=sQuery(id+"F0.wireOp",EDGE,"E6");var subQ3=sQuery(id+"F0.wireOp",EDGE,"E5");var subQ4=sQuery(id+"F0.wireOp",EDGE,"E4");var subQ5=sQuery(id+"F0.wireOp",EDGE,"E22.filletArc");var subQ6=sQuery(id+"F0.wireOp",EDGE,"E1.bottom");var subQ7=sQuery(id+"F0.wireOp",EDGE,"E1.right");var subQ8=sQuery(id+"F0.wireOp",EDGE,"E1.top");var subQ9=sQuery(id+"F0.wireOp",EDGE,"E1.left");var subQ10=sQuery(id+"F0.wireOp",EDGE,"E23.filletArc");var subQ11=sQuery(id+"F0.wireOp",EDGE,"E24.filletArc");Q0=makeQuery(id+"F2.boolean.opBoolean","SPLIT",FACE,{"disambiguationData":[TD([makeQuery(id+"F1.opExtrude","SWEPT_FACE",FACE,{"disambiguationData":[OSD([subQ6])]})])],"derivedFrom":makeQuery(id+"F1.opExtrude","CAP_FACE",FACE,{"disambiguationData":[OSD([subQ6,subQ8,subQ9,subQ7,subQ4,subQ3,subQ2,subQ1,subQ0,subQ5,subQ10,subQ11])],"isStart":true})});}
            var sketch = newSketch(context, id + "F16", { "sketchPlane" : qUnion([Q0])});
            skLineSegment(sketch, "E79", {"start": v(0, 74.25) * mm, "end": v(0, 104.25) * mm, "construction": true});
            skPoint(sketch, "E79.endSnap0", {"position": v(0, 74.25) * mm});
            skArc(sketch, "E80", {"start": v(15, 104.25) * mm, "mid": v(0, 119.25) * mm, "end": v(-15, 104.25) * mm});
            skLineSegment(sketch, "E81", {"start": v(15, 104.25) * mm, "end": v(15, 92.25) * mm});
            skLineSegment(sketch, "E82", {"start": v(-15, 104.25) * mm, "end": v(-15, 92.25) * mm});
            skLineSegment(sketch, "E83", {"start": v(-15, 92.25) * mm, "end": v(-33, 74.25) * mm});
            skLineSegment(sketch, "E84", {"start": v(15, 92.25) * mm, "end": v(33, 74.25) * mm});
            skCircle(sketch, "E85", {"center": v(0, 104.25) * mm, "radius": 6 * mm});
            skLineSegment(sketch, "E86", {"start": v(-74.25, 0) * mm, "end": v(74.25, 0) * mm, "construction": true});
            skLineSegment(sketch, "E87.MirrorCS", {"start": v(15, -104.25) * mm, "end": v(15, -92.25) * mm});
            skLineSegment(sketch, "E88.MirrorCS", {"start": v(-15, -104.25) * mm, "end": v(-15, -92.25) * mm});
            skLineSegment(sketch, "E89.MirrorCS", {"start": v(-15, -92.25) * mm, "end": v(-33, -74.25) * mm});
            skPoint(sketch, "E90.MirrorP", {"position": v(0, -74.25) * mm});
            skLineSegment(sketch, "E91.MirrorCS", {"start": v(0, -74.25) * mm, "end": v(0, -104.25) * mm, "construction": true});
            skArc(sketch, "E92.MirrorCS", {"start": v(15, -104.25) * mm, "mid": v(0, -119.25) * mm, "end": v(-15, -104.25) * mm});
            skCircle(sketch, "E93.MirrorC", {"center": v(0, -104.25) * mm, "radius": 6 * mm});
            skLineSegment(sketch, "E94.MirrorCS", {"start": v(15, -92.25) * mm, "end": v(33, -74.25) * mm});
            skSolve(sketch);
        }
        {
            var Q0;
            Q0=makeQuery(id+"F16.imprint","IMPRINT",FACE,{"disambiguationData":[TD([[makeQuery(id+"F16.imprint","IMPRINT",EDGE,{"derivedFrom":sQuery(id+"F16.wireOp",EDGE,"E80")}),1.0]])]});
            var Q1;
            Q1=makeQuery(id+"F16.imprint","IMPRINT",FACE,{"disambiguationData":[TD([[makeQuery(id+"F16.imprint","IMPRINT",EDGE,{"derivedFrom":makeQuery(id+"F1.opExtrude","CAP_EDGE",EDGE,{"disambiguationData":[OSD([sQuery(id+"F0.wireOp",EDGE,"E1.left")])],"isStart":true})}),-1.0]])]});
            var Q2;
            Q2=makeQuery(id+"F16.imprint","IMPRINT",FACE,{"disambiguationData":[TD([[makeQuery(id+"F16.imprint","IMPRINT",EDGE,{"derivedFrom":sQuery(id+"F16.wireOp",EDGE,"E87.MirrorCS")}),1.0]])]});
            var Q3;
            Q3=makeQuery(id+"F2.opExtrude","CAP_FACE",FACE,{"disambiguationData":[OSD([sQuery(id+"F0.wireOp",EDGE,"E12"),sQuery(id+"F0.wireOp",EDGE,"E13"),sQuery(id+"F0.wireOp",EDGE,"E14"),sQuery(id+"F0.wireOp",EDGE,"E15"),sQuery(id+"F0.wireOp",EDGE,"E17.filletArc"),sQuery(id+"F0.wireOp",EDGE,"E18.filletArc"),sQuery(id+"F0.wireOp",EDGE,"E19.filletArc"),sQuery(id+"F0.wireOp",EDGE,"E20.filletArc"),sQuery(id+"F0.wireOp",EDGE,"E25.0"),sQuery(id+"F0.wireOp",EDGE,"E25.1"),sQuery(id+"F0.wireOp",EDGE,"E25.2"),sQuery(id+"F0.wireOp",EDGE,"E25.3"),sQuery(id+"F0.wireOp",EDGE,"E25.4"),sQuery(id+"F0.wireOp",EDGE,"E25.5"),sQuery(id+"F0.wireOp",EDGE,"E25.6"),sQuery(id+"F0.wireOp",EDGE,"E25.7")])],"isStart":false});
            extrude(context, id + "F17", {"entities" : qUnion([Q0, Q1, Q2]), "endBound" : BoundingType.UP_TO_SURFACE, "endBoundEntityFace" : qUnion([Q3]), "depth" : 25 * mm});
        }
    });
